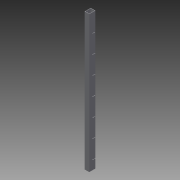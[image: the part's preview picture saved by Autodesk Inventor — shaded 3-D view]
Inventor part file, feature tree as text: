
AUTODESK INVENTOR PART (.ipt)
format: ipt  version: 2013 (Build 170138000, 138)  size: 124,416 bytes
history: native  units: in
note: dims shown in document units (in); Inventor stores cm internally (conversion verified against a paired STEP export)
features: other x4, extrude x1, sketch x1
ambient origin geometry x8: Origin, YZ Plane, XZ Plane, XY Plane, X Axis, Y Axis, Z Axis, Center Point
bodies: Solid1 (feature_tree)
feature tree (6):
  other  "Table"
  other  "squareTube1.5x2.ipt"
  extrude  "Extrusion1"  TaperAngle=0.0deg  [1 undecoded]
  other  "Solid1::squareTube1.5x2.ipt"
  other  "TaggingFeature1"
  sketch  "Sketch1"  dims[d0=1.5in d1=2.0in d2=0.125in d4=0.0in d3=0.25in d5=0.125in d6=6.0in d7=2.7559in d9=6.0in d10=0.3937in d12=1.0in d14=1.0in d15=0.0in]
note: 1 required parameter value undecoded (feature->parameter linkage not recoverable at this tier; creation-order binding heuristic only, values carry confidence <= 0.55)
